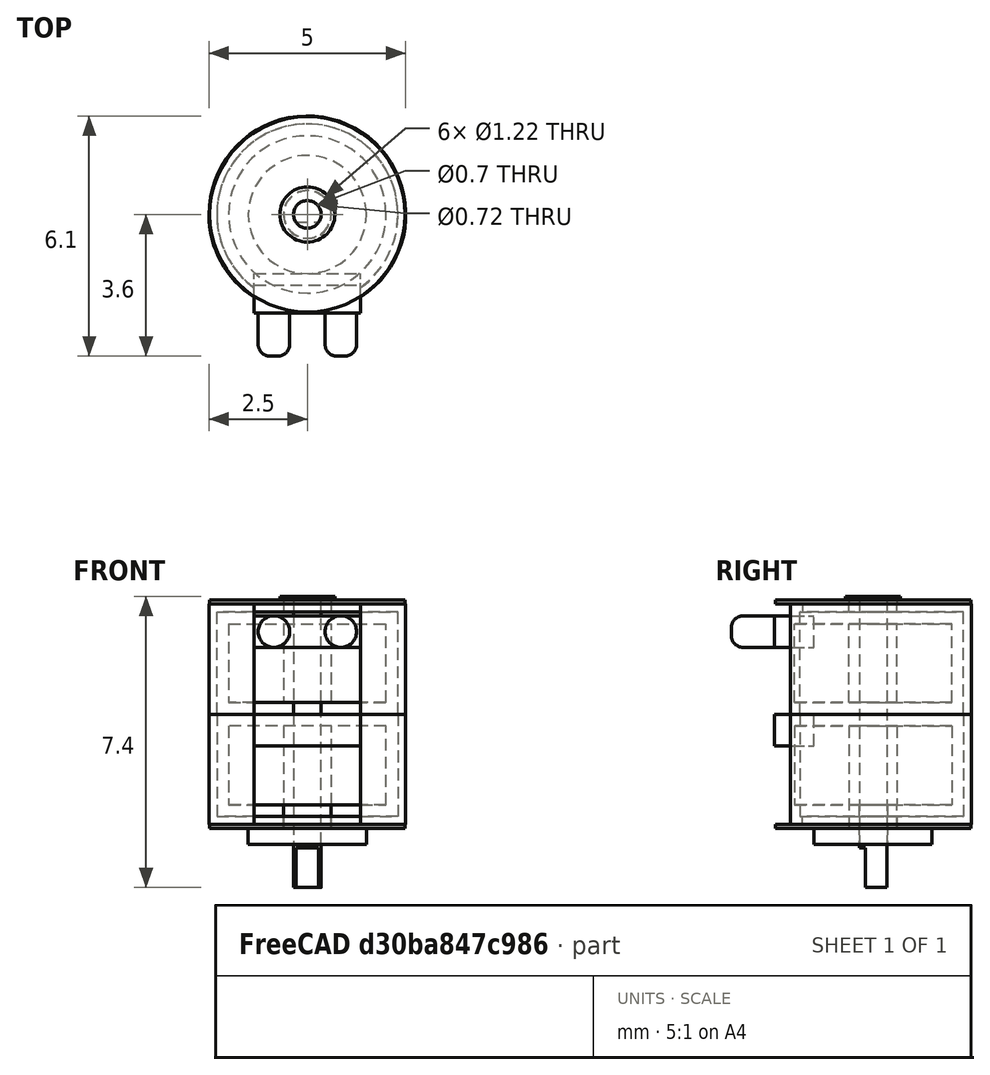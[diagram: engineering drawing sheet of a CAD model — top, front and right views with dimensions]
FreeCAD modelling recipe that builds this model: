
FCSTD DOCUMENT  (FreeCAD 1.0R39109 (Git))
Label: StepperMotor_4.7mm_Sanyo_ultra-mini
License: All rights reserved
LicenseURL: https://en.wikipedia.org/wiki/All_rights_reserved
objects: Part::Cylinder×9, Part::Cut×9, Part::Feature×5, Part::Box×2, App::Link×2, Part::FeaturePython×1, Part::Thickness×1, Sketcher::SketchObject×1, Part::Extrusion×1, Part::Compound×1, Part::Fillet×1, Assembly::JointGroup×1, PartDesign::FeatureBase×1, PartDesign::Body×1, App::Part×1, Assembly::AssemblyObject×1
note: 35 computed .brp shape members not serialized (recipe doc carries the construction recipe); baked Part::Feature solids carry a one-line shape summary decoded from their .brp

FEATURE [Part::Cylinder] Cylinder
  Angle = 360
  AttacherType = Attacher::AttachEngine3D
  FirstAngle = 0
  Height = 10
  Radius = 0.36
  SecondAngle = 0
FEATURE [Part::Cylinder] Cylinder001
  Angle = 360
  AttacherType = Attacher::AttachEngine3D
  FirstAngle = 0
  Height = 1
  Radius = 1.5
  SecondAngle = 0
FEATURE [Part::Cut] Cut
  Base = -> Cylinder001
  Refine = true
  Tool = -> Cylinder
FEATURE [Part::FeaturePython] Tube  # WARN: FeaturePython — macro-defined, semantics opaque (R4)
  AttacherType = Attacher::AttachEngine3D
  Height = 2
  InnerRadius = 0.6
  OuterRadius = 1.5
  Placement = pos=(0,0,0.4) rot=(0,0,1;0rad)
FEATURE [Part::Cut] Cut001  label="BushingFront"
  Base = -> Cut
  Refine = true
  Tool = -> Tube
FEATURE [Part::Cylinder] Cylinder002
  Angle = 360
  AttacherType = Attacher::AttachEngine3D
  FirstAngle = 0
  Height = 2.8
  Radius = 2.5
  SecondAngle = 0
FEATURE [Part::Thickness] Thickness
  Faces = -> Cylinder002 [Face3]
  Intersection = false
  Join = 0
  Mode = 0
  Placement = pos=(0,0,0.4) rot=(0,0,1;0rad)
  SelfIntersection = false
  Value = -0.2
FEATURE [Part::Cylinder] Cylinder003
  Angle = 360
  AttacherType = Attacher::AttachEngine3D
  FirstAngle = 0
  Height = 10
  Radius = 0.61
  SecondAngle = 0
FEATURE [Part::Cut] Cut002
  Base = -> Thickness
  Refine = true
  Tool = -> Cylinder003
FEATURE [Part::Box] Box  label="Cube"
  AttacherType = Attacher::AttachEngine3D
  Height = 10
  Length = 2.7
  Placement = pos=(-1.35,-4.5,0) rot=(0,0,1;0rad)
  Width = 2.7
FEATURE [Part::Cut] Cut003  label="BodyFront"
  Base = -> Cut002
  Placement = pos=(0,0,0.1) rot=(0,0,1;0rad)
  Refine = true
  Tool = -> Box
FEATURE [Part::Cylinder] Cylinder004
  Angle = 360
  AttacherType = Attacher::AttachEngine3D
  FirstAngle = 0
  Height = 0.1
  Placement = pos=(0,0,0.4) rot=(0,0,1;0rad)
  Radius = 2.48
  SecondAngle = 0
FEATURE [Part::Cut] Cut004  label="EndCapFront"
  Base = -> Cylinder004
  Refine = true
  Tool = -> Cylinder003
FEATURE [Part::Cylinder] Cylinder005
  Angle = 360
  AttacherType = Attacher::AttachEngine3D
  FirstAngle = 0
  Height = 7.3
  Placement = pos=(0,0,-1.1) rot=(0,0,1;0rad)
  Radius = 0.35
  SecondAngle = 0
FEATURE [Sketcher::SketchObject] Sketch
  ArcFitTolerance = 1e-06
  AttachmentSupport = -> [Cylinder005]
  ExternalGeometry = -> [Cylinder005]
  FullyConstrained = true
  MakeInternals = false
  MapMode = 2
  Placement = pos=(0,0,-1.1) rot=(0,0,1;0rad)
  sketch-geometry (2):
    g0: ArcOfCircle CenterX=0 CenterY=0 CenterZ=0 NormalX=0 NormalY=0 NormalZ=1 AngleXU=0 Radius=0.35 StartAngle=3.74984 EndAngle=5.67494
    g1: LineSegment StartX=-0.287228 StartY=-0.2 StartZ=0 EndX=0.287228 EndY=-0.2 EndZ=0
  constraints (6):
    c: Horizontal(g1)
    c: Coincident(g0,g-1)
    c: PointOnObject(g1,g-3)
    c: Distance(g0,g1) = 0.2
    c: Coincident(g0,g1)
    c: Coincident(g0,g1)
FEATURE [Part::Extrusion] Extrude004
  Base = -> Sketch
  Dir = (0,0,1)
  DirMode = 0
  FaceMakerClass = Part::FaceMakerBullseye
  FaceMakerMode = 3
  LengthFwd = 1
  LengthRev = 0
  Solid = true
  Symmetric = false
FEATURE [Part::Cut] Cut005  label="Shaft"
  Base = -> Cylinder005
  Refine = true
  Tool = -> Extrude004
FEATURE [Part::Cylinder] Cylinder006
  Angle = 360
  AttacherType = Attacher::AttachEngine3D
  FirstAngle = 0
  Height = 2
  Placement = pos=(0,0,1) rot=(0,0,1;0rad)
  Radius = 2
  SecondAngle = 0
FEATURE [Part::Cut] Cut006  label="CoilFront"
  Base = -> Cylinder006
  Refine = true
  Tool = -> Cylinder003
FEATURE [Part::Feature] Cut007  label="CoilRear"
  Placement = pos=(0,0,6.6) rot=(0,1,0;3.14159rad)
  shape: bbox 4 x 4 x 2 mm, 4 faces (baked)
FEATURE [Part::Feature] Cut008  label="BodyRear"
  Placement = pos=(0,0,6.5) rot=(0,1,0;3.14159rad)
  shape: bbox 5 x 4.604 x 2.8 mm, 9 faces (baked)
FEATURE [Part::Feature] Cut009  label="EndCapRear"
  Placement = pos=(0,0,6.6) rot=(0,1,0;3.14159rad)
  shape: bbox 4.96 x 4.96 x 0.1 mm, 4 faces (baked)
FEATURE [Part::Cylinder] Cylinder007
  Angle = 360
  AttacherType = Attacher::AttachEngine3D
  FirstAngle = 0
  Height = 0.2
  Placement = pos=(0,0,5.1) rot=(0,0,1;0rad)
  Radius = 0.7
  SecondAngle = 0
FEATURE [App::Link] Link  label="Shaft001"
  LinkedObject = -> Cut005
FEATURE [Part::Cut] Cut010
  Base = -> Cylinder007
  Placement = pos=(0,0,1) rot=(0,0,1;0rad)
  Refine = true
  Tool = -> Link
FEATURE [App::Link] Link001  label="EndCap002"
  LinkPlacement = pos=(0,0,5.7) rot=(0,0,1;0rad)
  LinkedObject = -> Cut009
  Placement = pos=(0,0,5.7) rot=(0,0,1;0rad)
FEATURE [Part::Cut] Cut011  label="BushingRear"
  Base = -> Cut010
  Refine = true
  Tool = -> Link001
FEATURE [Part::Box] Box001  label="ConnectorBlockFront"
  AttacherType = Attacher::AttachEngine3D
  Height = 0.8
  Length = 2.7
  Placement = pos=(-1.35,-2.5,2.5) rot=(0,0,1;0rad)
  Width = 1
FEATURE [Part::Feature] Box002  label="ConnectorBlockRear"
  Placement = pos=(-1.35,-2.5,5) rot=(0,0,1;0rad)
  shape: bbox 2.7 x 1 x 0.8 mm, 6 faces (baked)
FEATURE [Part::Cylinder] Cylinder008
  Angle = 360
  AttacherType = Attacher::AttachEngine3D
  FirstAngle = 0
  Height = 1.1
  Placement = pos=(-0.85,-2.5,2.9) rot=(1,0,0;1.5708rad)
  Radius = 0.4
  SecondAngle = 0
FEATURE [Part::Feature] Cylinder009
  Placement = pos=(0.85,-2.5,2.9) rot=(1,0,0;1.5708rad)
  shape: bbox 0.8 x 1.1 x 0.8 mm, 3 faces (baked)
FEATURE [Part::Compound] Compound
  Links = -> [Cylinder008,Cylinder009]
FEATURE [Part::Fillet] Fillet  label="PinsFront"
  Base = -> Compound
  EdgeLinks = -> Compound [Edge3,Edge6]
  Edges = 2 edges r=0.3: [Edge3,Edge6]
FEATURE [Assembly::JointGroup] Joints
FEATURE [PartDesign::FeatureBase] Clone
  BaseFeature = -> Fillet
  Suppressed = false
FEATURE [PartDesign::Body] Body  label="PinsRear"
  AllowCompound = false
  Group = -> [Clone]
  Origin = -> Origin002
  Placement = pos=(0,0,2.5) rot=(0,0,1;0rad)
  Tip = -> Clone
FEATURE [App::Part] Part
  Group = -> [Cylinder,Cut,Tube,Cylinder001,Cut001,Cut002,Cut004,Cut006,Box,Cylinder006,Thickness,Cylinder004,Cylinder003,Cylinder002,Cut003,Extrude004,Cylinder005,Sketch,Cut005,Cut007,Cut008,Cut009,Cut010,Cylinder007,Link,Link001,Cut011,Box001,Box002,Cylinder009,Compound,Cylinder008,Fillet,Body]
  Origin = -> Origin
  Placement = pos=(4.25,0,2.5) rot=(0.57735,-0.57735,-0.57735;2.0944rad)
FEATURE [Assembly::AssemblyObject] Assembly
  Group = -> [Joints,Part]
  Origin = -> Origin001
  Type = Assembly
